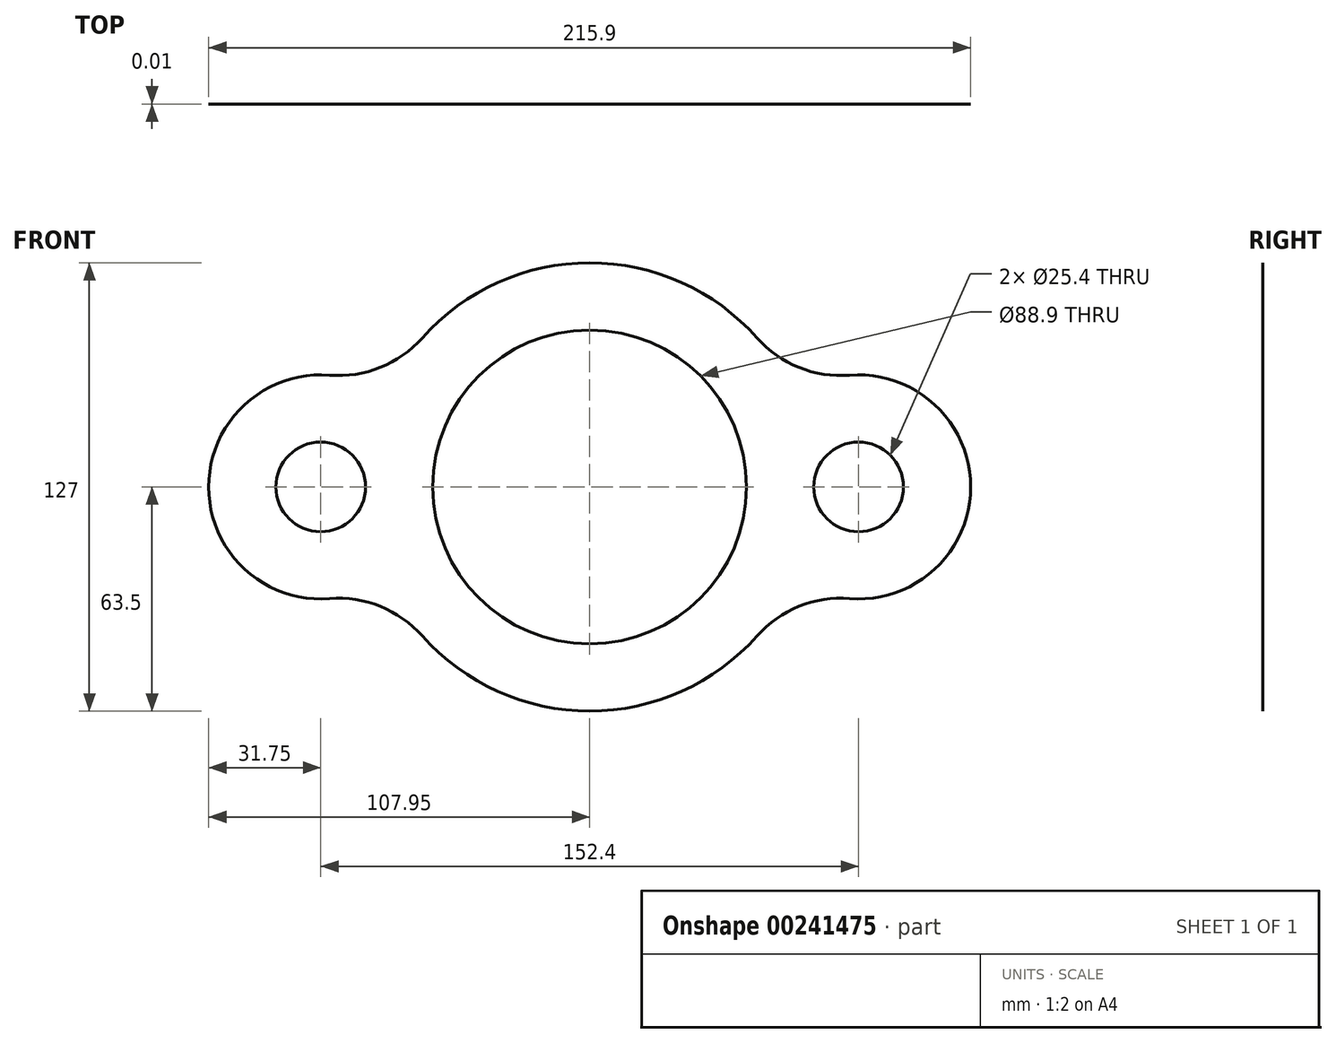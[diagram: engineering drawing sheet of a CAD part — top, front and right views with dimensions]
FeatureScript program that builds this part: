
annotation { "Feature Type Name" : "Feature", "Feature Type Description" : "" }
export const myFeature = defineFeature(function(context is Context, id is Id, definition is map)
    precondition{}
    {
        {
            var Q0;
            Q0=qCreatedBy(makeId("Front.planeOp"),FACE);
            var sketch = newSketch(context, id + "F0", { "sketchPlane" : qUnion([Q0])});
            skCircle(sketch, "E0", {"center": v(0, 0) * mm, "radius": 44.45 * mm});
            skCircle(sketch, "E1", {"center": v(76.2, 0) * mm, "radius": 12.7 * mm});
            skCircle(sketch, "E2", {"center": v(-76.2, 0) * mm, "radius": 12.7 * mm});
            skArc(sketch, "E3", {"start": v(-47.45, -42.2) * mm, "mid": v(0, -63.5) * mm, "end": v(47.45, -42.2) * mm});
            skArc(sketch, "E4", {"start": v(73.69, -31.65) * mm, "mid": v(107.95, 0) * mm, "end": v(73.69, 31.65) * mm});
            skArc(sketch, "E5", {"start": v(-73.69, 31.65) * mm, "mid": v(-107.95, 0) * mm, "end": v(-73.69, -31.65) * mm});
            skArc(sketch, "E6.trimOffspring", {"start": v(47.45, 42.2) * mm, "mid": v(0, 63.5) * mm, "end": v(-47.45, 42.2) * mm});
            skPoint(sketch, "E7.visualSharp", {"position": v(-57.94, 25.98) * mm});
            skArc(sketch, "E7.filletArc", {"start": v(-73.69, 31.65) * mm, "mid": v(-59.33, 33.84) * mm, "end": v(-47.45, 42.2) * mm});
            skPoint(sketch, "E8.visualSharp", {"position": v(-57.94, -25.98) * mm});
            skArc(sketch, "E8.filletArc", {"start": v(-47.45, -42.2) * mm, "mid": v(-59.33, -33.84) * mm, "end": v(-73.69, -31.65) * mm});
            skPoint(sketch, "E9.visualSharp", {"position": v(57.94, -25.98) * mm});
            skArc(sketch, "E9.filletArc", {"start": v(73.69, -31.65) * mm, "mid": v(59.33, -33.84) * mm, "end": v(47.45, -42.2) * mm});
            skPoint(sketch, "E10.visualSharp", {"position": v(57.94, 25.98) * mm});
            skArc(sketch, "E10.filletArc", {"start": v(47.45, 42.2) * mm, "mid": v(59.33, 33.84) * mm, "end": v(73.69, 31.65) * mm});
            skSolve(sketch);
        }
        {
            var Q0;
            Q0=makeQuery(id+"F0.imprint","IMPRINT",FACE,{"disambiguationData":[TD([[makeQuery(id+"F0.imprint","IMPRINT",EDGE,{"derivedFrom":sQuery(id+"F0.wireOp",EDGE,"E0")}),-1.0]])]});
            extrude(context, id + "F1", {"entities" : qUnion([Q0]), "depth" : 1 / 101.6 * mm});
        }
    });
